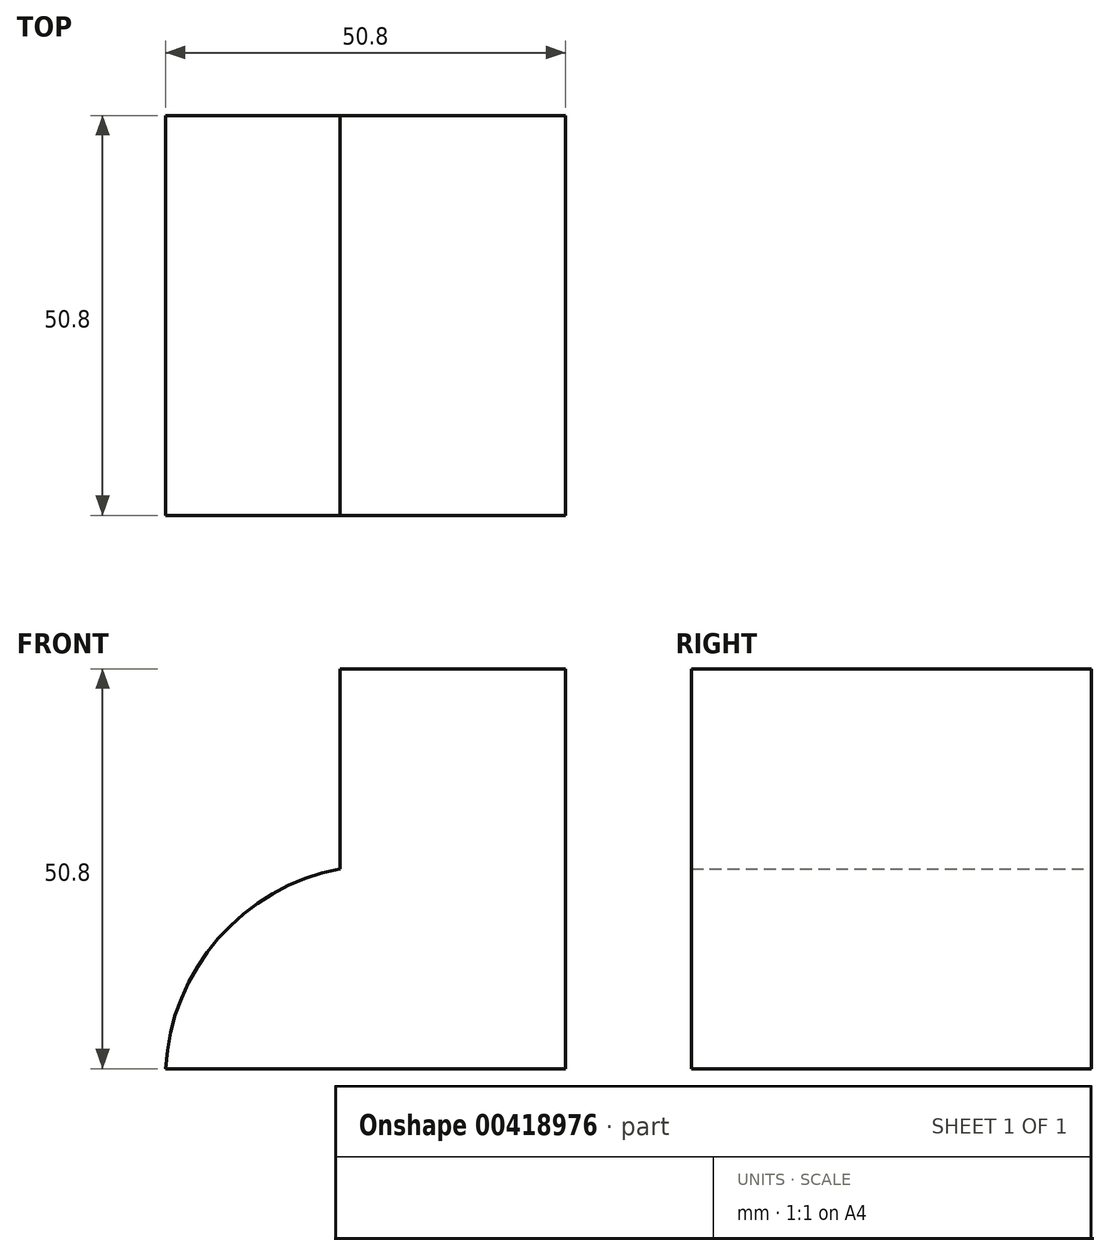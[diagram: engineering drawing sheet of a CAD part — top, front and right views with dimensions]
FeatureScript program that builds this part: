
annotation { "Feature Type Name" : "Feature", "Feature Type Description" : "" }
export const myFeature = defineFeature(function(context is Context, id is Id, definition is map)
    precondition{}
    {
        {
            var Q0;
            Q0=qCreatedBy(makeId("Front.planeOp"),FACE);
            var sketch = newSketch(context, id + "F0", { "sketchPlane" : qUnion([Q0])});
            skLineSegment(sketch, "E0", {"start": v(-50.8, 0) * mm, "end": v(0, 0) * mm});
            skLineSegment(sketch, "E1", {"start": v(0, 0) * mm, "end": v(0, 50.8) * mm});
            skLineSegment(sketch, "E2", {"start": v(0, 50.8) * mm, "end": v(-28.64, 50.8) * mm});
            skLineSegment(sketch, "E3", {"start": v(-28.64, 50.8) * mm, "end": v(-28.64, 25.4) * mm});
            skArc(sketch, "E4", {"start": v(-28.64, 25.4) * mm, "mid": v(-44.1, 16.52) * mm, "end": v(-50.8, 0) * mm});
            skSolve(sketch);
        }
        {
            var Q0;
            Q0 = qSketchRegion(id + "F0", true);
            extrude(context, id + "F1", {"entities" : qUnion([Q0]), "depth" : 50.8 * mm});
        }
    });
